# Revit family: Haworth_ActiveComponents_SuspendedEnder_BUILD
name_source: partatom
category: Furniture Systems
revit_build: Autodesk Revit Architecture 2015 (Build: 20141119_1515(x64)
units: mm (PartAtom-declared; Revit-internal decimal feet)

## types (4) — shared parameters
Actual Depth = 9"
Actual Height = 18"
Actual Mounting Height = 29"
Assembly Code = E2020200
Manufacturer = Haworth
Max. Width = 63"
Min. Width = 51"
Model = AHEA, AHEC
Revision Number = 1
Size = Verify Final Dim. w/ Haworth
Sustainability Info = https://www.haworth.com
URL = http://www.haworth.com
URL - Product = http://www.haworth.com
Warranty = http://www.haworth.com

## per-type parameters (varying)
| type | Actual Width | Box File | Description | Drawer Height | Open with Box Drawer | Width |
| 51w - Box File | 51" | Yes | Haworth Active Components Suspended Ender - Box File - 51w | 18" | No | 51" |
| 63w - Box File | 63" | Yes | Haworth Active Components Suspended Ender - Box File - 63w | 18" | No | 63" |
| 51w - Open with Box Drawer | 51" | No | Haworth Active Components Suspended Ender - Open with Box Drawer - 51w | 3 15/16" | Yes | 51" |
| 63w - Open with Box Drawer | 63" | No | Haworth Active Components Suspended Ender - Open with Box Drawer - 63w | 3 15/16" | Yes | 63" |

## geometry (parser evidence)
native form markers: Blend x2, Sweep x3
no freeform markers — native parametric forms only
